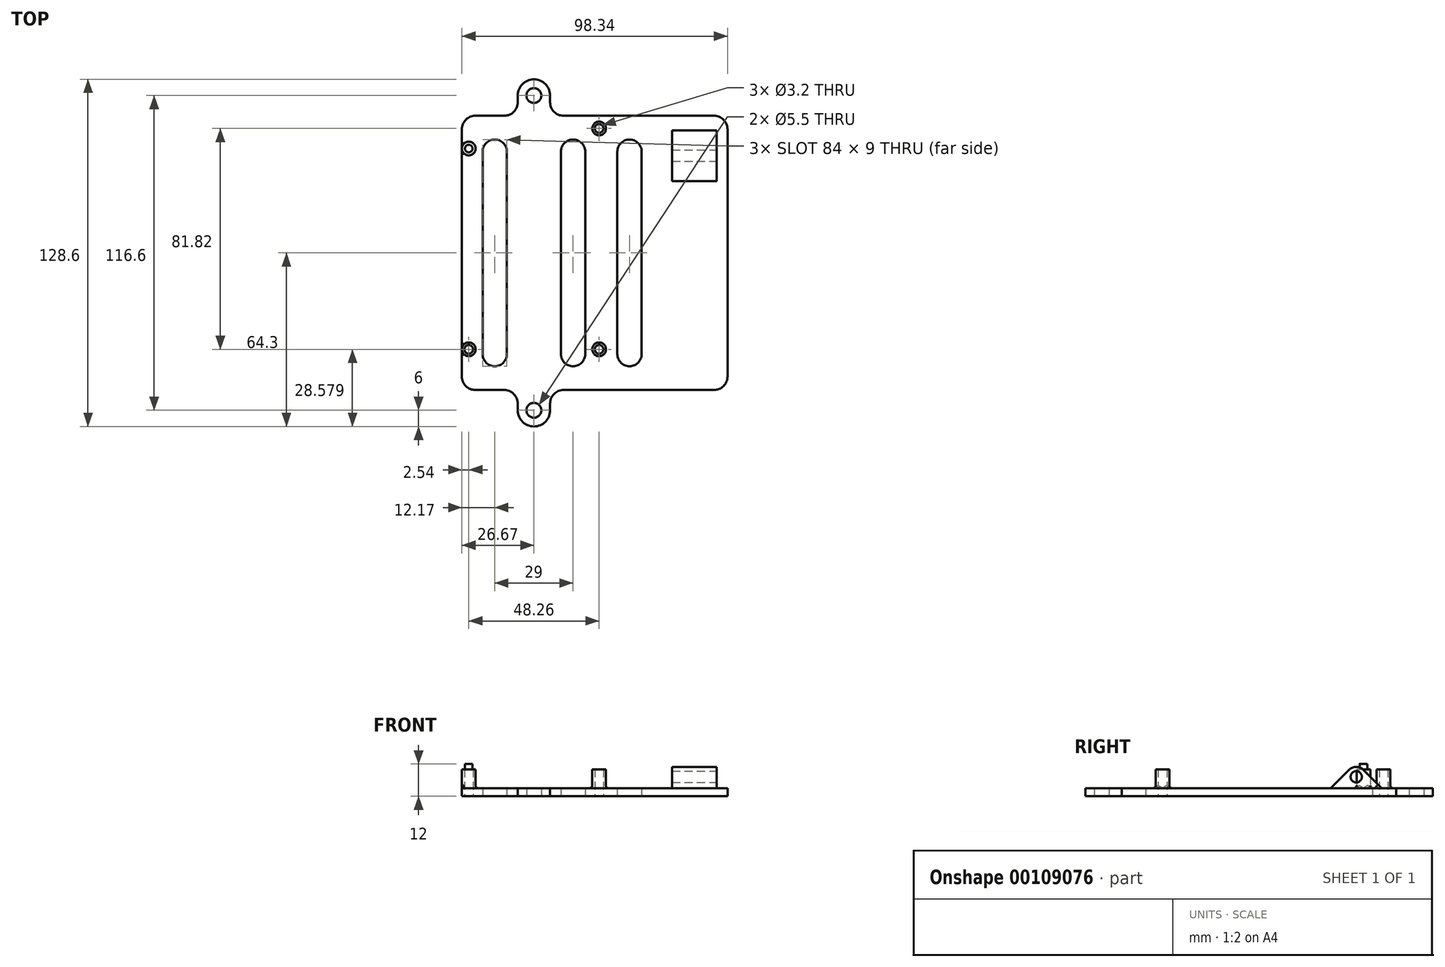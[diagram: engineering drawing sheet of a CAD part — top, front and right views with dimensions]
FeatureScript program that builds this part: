
annotation { "Feature Type Name" : "Feature", "Feature Type Description" : "" }
export const myFeature = defineFeature(function(context is Context, id is Id, definition is map)
    precondition{}
    {
        {
            var Q0;
            Q0=qCreatedBy(makeId("Top.planeOp"),FACE);
            var sketch = newSketch(context, id + "F0", { "sketchPlane" : qUnion([Q0])});
            skLineSegment(sketch, "E0.bottom", {"start": v(26.67, -50.8) * mm, "end": v(-26.67, -50.8) * mm});
            skLineSegment(sketch, "E0.top", {"start": v(26.67, 50.8) * mm, "end": v(-26.67, 50.8) * mm});
            skLineSegment(sketch, "E0.left", {"start": v(26.67, -50.8) * mm, "end": v(26.67, 50.8) * mm});
            skLineSegment(sketch, "E0.right", {"start": v(-26.67, -50.8) * mm, "end": v(-26.67, 50.8) * mm});
            skPoint(sketch, "E0.middle", {"position": v(0, 0) * mm});
            skLineSegment(sketch, "E1.bottom", {"start": v(-24.13, 46.1) * mm, "end": v(24.13, 46.1) * mm, "construction": true});
            skLineSegment(sketch, "E1.top", {"start": v(-24.13, -35.72) * mm, "end": v(24.13, -35.72) * mm, "construction": true});
            skLineSegment(sketch, "E1.left", {"start": v(-24.13, 46.1) * mm, "end": v(-24.13, -35.72) * mm, "construction": true});
            skLineSegment(sketch, "E1.right", {"start": v(24.13, 46.1) * mm, "end": v(24.13, -35.72) * mm, "construction": true});
            skPoint(sketch, "E2", {"position": v(-24.13, 38.67) * mm});
            skLineSegment(sketch, "E3", {"start": v(0, 0) * mm, "end": v(0, 72.43) * mm, "construction": true});
            skPoint(sketch, "E4", {"position": v(0, -35.72) * mm});
            skCircle(sketch, "E5", {"center": v(-24.13, -35.72) * mm, "radius": 1.6 * mm});
            skCircle(sketch, "E6", {"center": v(24.13, -35.72) * mm, "radius": 1.6 * mm});
            skCircle(sketch, "E7", {"center": v(24.13, 46.1) * mm, "radius": 1.6 * mm});
            skCircle(sketch, "E8", {"center": v(24.13, 46.1) * mm, "radius": 2.54 * mm});
            skCircle(sketch, "E9", {"center": v(-24.13, 38.67) * mm, "radius": 2.54 * mm});
            skCircle(sketch, "E10", {"center": v(24.13, -35.72) * mm, "radius": 2.54 * mm});
            skCircle(sketch, "E11", {"center": v(-24.13, -35.72) * mm, "radius": 2.54 * mm});
            skLineSegment(sketch, "E12", {"start": v(-6, 50.8) * mm, "end": v(-6, 58.3) * mm});
            skArc(sketch, "E13", {"start": v(6, 58.3) * mm, "mid": v(0, 64.3) * mm, "end": v(-6, 58.3) * mm});
            skLineSegment(sketch, "E14", {"start": v(6, 58.3) * mm, "end": v(6, 50.8) * mm});
            skCircle(sketch, "E15", {"center": v(0, 58.3) * mm, "radius": 2.75 * mm});
            skLineSegment(sketch, "E16", {"start": v(-66.86, 0) * mm, "end": v(84.73, 0) * mm, "construction": true});
            skLineSegment(sketch, "E17.MirrorCS", {"start": v(6, -58.3) * mm, "end": v(6, -50.8) * mm});
            skLineSegment(sketch, "E18.MirrorCS", {"start": v(-6, -50.8) * mm, "end": v(-6, -58.3) * mm});
            skCircle(sketch, "E19.MirrorC", {"center": v(0, -58.3) * mm, "radius": 2.75 * mm});
            skArc(sketch, "E20.MirrorCS", {"start": v(6, -58.3) * mm, "mid": v(0, -64.3) * mm, "end": v(-6, -58.3) * mm});
            skLineSegment(sketch, "E21", {"start": v(19, -37.5) * mm, "end": v(19, 37.5) * mm});
            skPoint(sketch, "E22", {"position": v(19, 0) * mm});
            skLineSegment(sketch, "E23", {"start": v(10, -37.5) * mm, "end": v(10, 37.5) * mm});
            skPoint(sketch, "E24", {"position": v(10, 0) * mm});
            skArc(sketch, "E25", {"start": v(19, -37.5) * mm, "mid": v(14.5, -42) * mm, "end": v(10, -37.5) * mm});
            skArc(sketch, "E26", {"start": v(10, 37.5) * mm, "mid": v(14.5, 42) * mm, "end": v(19, 37.5) * mm});
            skLineSegment(sketch, "E27.direction1", {"start": v(10, -37.5) * mm, "end": v(-4, -37.5) * mm, "construction": true});
            skLineSegment(sketch, "E28.bottom", {"start": v(26.67, 50.8) * mm, "end": v(71.67, 50.8) * mm});
            skLineSegment(sketch, "E28.top", {"start": v(26.67, -50.8) * mm, "end": v(71.67, -50.8) * mm});
            skLineSegment(sketch, "E28.left", {"start": v(26.67, 50.8) * mm, "end": v(26.67, -50.8) * mm});
            skLineSegment(sketch, "E28.right", {"start": v(71.67, 50.8) * mm, "end": v(71.67, -50.8) * mm});
            skLineSegment(sketch, "E29", {"start": v(30.9, -37.5) * mm, "end": v(30.9, 37.5) * mm});
            skLineSegment(sketch, "E30", {"start": v(39.9, 37.5) * mm, "end": v(39.9, -37.5) * mm});
            skArc(sketch, "E31", {"start": v(39.9, 37.5) * mm, "mid": v(35.4, 42) * mm, "end": v(30.9, 37.5) * mm});
            skArc(sketch, "E32", {"start": v(30.9, -37.5) * mm, "mid": v(35.4, -42) * mm, "end": v(39.9, -37.5) * mm});
            skLineSegment(sketch, "E33.MirrorCS", {"start": v(-10, -37.5) * mm, "end": v(-10, 37.5) * mm});
            skArc(sketch, "E34.MirrorCS", {"start": v(-10, 37.5) * mm, "mid": v(-14.5, 42) * mm, "end": v(-19, 37.5) * mm});
            skLineSegment(sketch, "E35.MirrorCS", {"start": v(-19, -37.5) * mm, "end": v(-19, 37.5) * mm});
            skArc(sketch, "E36.MirrorCS", {"start": v(-19, -37.5) * mm, "mid": v(-14.5, -42) * mm, "end": v(-10, -37.5) * mm});
            skSolve(sketch);
        }
        {
            var Q0;
            {var subQ5=sQuery(id+"F0.wireOp",EDGE,"E0.bottom");Q0=makeQuery(id+"F0.imprint","IMPRINT",FACE,{"disambiguationData":[TD([[makeQuery(id+"F0.imprint","IMPRINT",EDGE,{"derivedFrom":subQ5}),-1.0]])]});}
            var Q1;
            Q1=makeQuery(id+"F0.imprint","IMPRINT",FACE,{"disambiguationData":[TD([[makeQuery(id+"F0.imprint","IMPRINT",EDGE,{"derivedFrom":sQuery(id+"F0.wireOp",EDGE,"E5")}),-1.0]])]});
            var Q2;
            Q2=makeQuery(id+"F0.imprint","IMPRINT",FACE,{"disambiguationData":[TD([[makeQuery(id+"F0.imprint","IMPRINT",EDGE,{"derivedFrom":sQuery(id+"F0.wireOp",EDGE,"E6")}),-1.0]])]});
            var Q3;
            Q3=makeQuery(id+"F0.imprint","IMPRINT",FACE,{"disambiguationData":[TD([[makeQuery(id+"F0.imprint","IMPRINT",EDGE,{"derivedFrom":sQuery(id+"F0.wireOp",EDGE,"E7")}),-1.0]])]});
            var Q4;
            Q4=makeQuery(id+"F0.imprint","IMPRINT",FACE,{"disambiguationData":[TD([[makeQuery(id+"F0.imprint","IMPRINT",EDGE,{"derivedFrom":sQuery(id+"F0.wireOp",EDGE,"E9")}),1.0]])]});
            var Q5;
            {var subQ1=sQuery(id+"F0.wireOp",EDGE,"E12");Q5=makeQuery(id+"F0.imprint","IMPRINT",FACE,{"disambiguationData":[TD([[makeQuery(id+"F0.imprint","IMPRINT",EDGE,{"derivedFrom":subQ1}),-1.0]])]});}
            var Q6;
            {var subQ1=sQuery(id+"F0.wireOp",EDGE,"E17.MirrorCS");Q6=makeQuery(id+"F0.imprint","IMPRINT",FACE,{"disambiguationData":[TD([[makeQuery(id+"F0.imprint","IMPRINT",EDGE,{"derivedFrom":subQ1}),1.0]])]});}
            var Q7;
            {var subQ3=sQuery(id+"F0.wireOp",EDGE,"E28.bottom");Q7=makeQuery(id+"F0.imprint","IMPRINT",FACE,{"disambiguationData":[TD([[makeQuery(id+"F0.imprint","IMPRINT",EDGE,{"derivedFrom":subQ3}),-1.0]])]});}
            extrude(context, id + "F1", {"entities" : qUnion([Q0, Q1, Q2, Q3, Q4, Q5, Q6, Q7]), "depth" : 3 * mm});
        }
        {
            var Q0;
            Q0=makeQuery(id+"F0.imprint","IMPRINT",FACE,{"disambiguationData":[TD([[makeQuery(id+"F0.imprint","IMPRINT",EDGE,{"derivedFrom":sQuery(id+"F0.wireOp",EDGE,"E7")}),-1.0]])]});
            var Q1;
            Q1=makeQuery(id+"F0.imprint","IMPRINT",FACE,{"disambiguationData":[TD([[makeQuery(id+"F0.imprint","IMPRINT",EDGE,{"derivedFrom":sQuery(id+"F0.wireOp",EDGE,"E9")}),1.0]])]});
            var Q2;
            Q2=makeQuery(id+"F0.imprint","IMPRINT",FACE,{"disambiguationData":[TD([[makeQuery(id+"F0.imprint","IMPRINT",EDGE,{"derivedFrom":sQuery(id+"F0.wireOp",EDGE,"E5")}),-1.0]])]});
            var Q3;
            Q3=makeQuery(id+"F0.imprint","IMPRINT",FACE,{"disambiguationData":[TD([[makeQuery(id+"F0.imprint","IMPRINT",EDGE,{"derivedFrom":sQuery(id+"F0.wireOp",EDGE,"E6")}),-1.0]])]});
            extrude(context, id + "F2", {"entities" : qUnion([Q0, Q1, Q2, Q3]), "operationType" : NewBodyOperationType.ADD, "depth" : 10 * mm});
        }
        {
            var Q0;
            Q0=makeQuery(id+"F2.opExtrude","CAP_FACE",FACE,{"disambiguationData":[OSD([sQuery(id+"F0.wireOp",EDGE,"E9")])],"isStart":false});
            var sketch = newSketch(context, id + "F3", { "sketchPlane" : qUnion([Q0])});
            skCircle(sketch, "E37", {"center": v(-24.13, 38.67) * mm, "radius": 1.4 * mm});
            skSolve(sketch);
        }
        {
            var Q0;
            Q0 = qSketchRegion(id + "F3", true);
            extrude(context, id + "F4", {"entities" : qUnion([Q0]), "operationType" : NewBodyOperationType.ADD, "depth" : 2 * mm});
        }
        {
            var Q0;
            Q0=makeQuery(id+"F1.opExtrude","SWEPT_EDGE",EDGE,{"disambiguationData":[OSD([sQuery(id+"F0.wireOp",EDGE,"E0.top"),sQuery(id+"F0.wireOp",EDGE,"E0.left")])]});
            var Q1;
            Q1=makeQuery(id+"F1.opExtrude","SWEPT_EDGE",EDGE,{"disambiguationData":[OSD([sQuery(id+"F0.wireOp",EDGE,"E0.top"),sQuery(id+"F0.wireOp",EDGE,"E14")])]});
            var Q2;
            Q2=makeQuery(id+"F1.opExtrude","SWEPT_EDGE",EDGE,{"disambiguationData":[OSD([sQuery(id+"F0.wireOp",EDGE,"E0.top"),sQuery(id+"F0.wireOp",EDGE,"E12")])]});
            var Q3;
            Q3=makeQuery(id+"F1.opExtrude","SWEPT_EDGE",EDGE,{"disambiguationData":[OSD([sQuery(id+"F0.wireOp",EDGE,"E0.top"),sQuery(id+"F0.wireOp",EDGE,"E0.right")])]});
            var Q4;
            Q4=makeQuery(id+"F1.opExtrude","SWEPT_EDGE",EDGE,{"disambiguationData":[OSD([sQuery(id+"F0.wireOp",EDGE,"E0.bottom"),sQuery(id+"F0.wireOp",EDGE,"E0.right")])]});
            var Q5;
            Q5=makeQuery(id+"F1.opExtrude","SWEPT_EDGE",EDGE,{"disambiguationData":[OSD([sQuery(id+"F0.wireOp",EDGE,"E0.bottom"),sQuery(id+"F0.wireOp",EDGE,"E18.MirrorCS")])]});
            var Q6;
            Q6=makeQuery(id+"F1.opExtrude","SWEPT_EDGE",EDGE,{"disambiguationData":[OSD([sQuery(id+"F0.wireOp",EDGE,"E0.bottom"),sQuery(id+"F0.wireOp",EDGE,"E17.MirrorCS")])]});
            var Q7;
            Q7=makeQuery(id+"F1.opExtrude","SWEPT_EDGE",EDGE,{"disambiguationData":[OSD([sQuery(id+"F0.wireOp",EDGE,"E0.bottom"),sQuery(id+"F0.wireOp",EDGE,"E0.left")])]});
            fillet(context, id + "F5", {"entities" : qUnion([Q0, Q1, Q2, Q3, Q4, Q5, Q6, Q7]), "radius" : 5 * mm, "tangentPropagation" : true, "allowEdgeOverflow" : false});
        }
        {
            var Q0;
            Q0=makeQuery(id+"F1.opExtrude","SWEPT_FACE",FACE,{"disambiguationData":[OSD([sQuery(id+"F0.wireOp",EDGE,"E28.right")])]});
            var sketch = newSketch(context, id + "F6", { "sketchPlane" : qUnion([Q0])});
            skLineSegment(sketch, "E38.0", {"start": v(50.8, 3) * mm, "end": v(-50.8, 3) * mm, "construction": true});
            skLineSegment(sketch, "E39", {"start": v(26.57, 3) * mm, "end": v(33.38, 9.82) * mm});
            skLineSegment(sketch, "E40", {"start": v(45.43, 3) * mm, "end": v(38.62, 9.82) * mm});
            skArc(sketch, "E41", {"start": v(38.62, 9.82) * mm, "mid": v(36, 10.9) * mm, "end": v(33.38, 9.82) * mm});
            skLineSegment(sketch, "E42", {"start": v(0, 30.22) * mm, "end": v(0, -10.95) * mm, "construction": true});
            skLineSegment(sketch, "E43", {"start": v(26.57, 3) * mm, "end": v(45.43, 3) * mm});
            skArc(sketch, "E44.MirrorCS", {"start": v(-38.62, 9.82) * mm, "mid": v(-36, 10.9) * mm, "end": v(-33.38, 9.82) * mm});
            skLineSegment(sketch, "E45.MirrorCS", {"start": v(-26.57, 3) * mm, "end": v(-33.38, 9.82) * mm});
            skLineSegment(sketch, "E46.MirrorCS", {"start": v(-26.57, 3) * mm, "end": v(-45.43, 3) * mm});
            skLineSegment(sketch, "E47.MirrorCS", {"start": v(-45.43, 3) * mm, "end": v(-38.62, 9.82) * mm});
            skCircle(sketch, "E48", {"center": v(36, 7.2) * mm, "radius": 2.1 * mm});
            skCircle(sketch, "E49.MirrorC", {"center": v(-36, 7.2) * mm, "radius": 2.1 * mm});
            skSolve(sketch);
        }
        {
            var Q0;
            Q0=makeQuery(id+"F6.imprint","IMPRINT",FACE,{"disambiguationData":[TD([[makeQuery(id+"F6.imprint","IMPRINT",EDGE,{"derivedFrom":sQuery(id+"F6.wireOp",EDGE,"E39")}),-1.0]])]});
            var Q1;
            Q1=makeQuery(id+"F6.imprint","IMPRINT",FACE,{"disambiguationData":[TD([[makeQuery(id+"F6.imprint","IMPRINT",EDGE,{"derivedFrom":sQuery(id+"F6.wireOp",EDGE,"E44.MirrorCS")}),-1.0]])]});
            extrude(context, id + "F7", {"entities" : qUnion([Q0, Q1]), "operationType" : NewBodyOperationType.ADD, "oppositeDirection" : true, "depth" : 20.5 * mm, "hasSecondDirection" : true, "secondDirectionOppositeDirection" : true, "secondDirectionDepth" : 4 * mm});
        }
        {
            var Q0;
            Q0=makeQuery(id+"F1.opExtrude","SWEPT_EDGE",EDGE,{"disambiguationData":[OSD([sQuery(id+"F0.wireOp",EDGE,"E28.top"),sQuery(id+"F0.wireOp",EDGE,"E28.right")])]});
            var Q1;
            Q1=makeQuery(id+"F7.opExtrude","SWEPT_EDGE",EDGE,{"disambiguationData":[OSD([sQuery(id+"F0.wireOp",EDGE,"E28.right"),sQuery(id+"F6.wireOp",EDGE,"E46.MirrorCS"),sQuery(id+"F6.wireOp",EDGE,"E47.MirrorCS")])]});
            var Q2;
            Q2=makeQuery(id+"F7.opExtrude","SWEPT_EDGE",EDGE,{"disambiguationData":[OSD([sQuery(id+"F0.wireOp",EDGE,"E28.right"),sQuery(id+"F6.wireOp",EDGE,"E45.MirrorCS"),sQuery(id+"F6.wireOp",EDGE,"E46.MirrorCS")])]});
            var Q3;
            Q3=makeQuery(id+"F7.opExtrude","SWEPT_EDGE",EDGE,{"disambiguationData":[OSD([sQuery(id+"F0.wireOp",EDGE,"E28.right"),sQuery(id+"F6.wireOp",EDGE,"E39"),sQuery(id+"F6.wireOp",EDGE,"E43")])]});
            var Q4;
            Q4=makeQuery(id+"F7.opExtrude","SWEPT_EDGE",EDGE,{"disambiguationData":[OSD([sQuery(id+"F0.wireOp",EDGE,"E28.right"),sQuery(id+"F6.wireOp",EDGE,"E40"),sQuery(id+"F6.wireOp",EDGE,"E43")])]});
            var Q5;
            Q5=makeQuery(id+"F1.opExtrude","SWEPT_EDGE",EDGE,{"disambiguationData":[OSD([sQuery(id+"F0.wireOp",EDGE,"E28.bottom"),sQuery(id+"F0.wireOp",EDGE,"E28.right")])]});
            fillet(context, id + "F8", {"entities" : qUnion([Q0, Q1, Q2, Q3, Q4, Q5]), "radius" : 5 * mm, "tangentPropagation" : true, "allowEdgeOverflow" : false});
        }
        {
            var Q0;
            Q0=makeQuery(id+"F2.boolean.opBoolean","INTERSECT",EDGE,{"derivedFrom":[makeQuery(id+"F1.opExtrude","CAP_FACE",FACE,{"disambiguationData":[OSD([sQuery(id+"F0.wireOp",EDGE,"E0.bottom"),sQuery(id+"F0.wireOp",EDGE,"E0.top"),sQuery(id+"F0.wireOp",EDGE,"E0.right"),sQuery(id+"F0.wireOp",EDGE,"E5"),sQuery(id+"F0.wireOp",EDGE,"E6"),sQuery(id+"F0.wireOp",EDGE,"E7"),sQuery(id+"F0.wireOp",EDGE,"E12"),sQuery(id+"F0.wireOp",EDGE,"E13"),sQuery(id+"F0.wireOp",EDGE,"E14"),sQuery(id+"F0.wireOp",EDGE,"E15"),sQuery(id+"F0.wireOp",EDGE,"E17.MirrorCS"),sQuery(id+"F0.wireOp",EDGE,"E18.MirrorCS"),sQuery(id+"F0.wireOp",EDGE,"E19.MirrorC"),sQuery(id+"F0.wireOp",EDGE,"E20.MirrorCS"),sQuery(id+"F0.wireOp",EDGE,"E21"),sQuery(id+"F0.wireOp",EDGE,"E23"),sQuery(id+"F0.wireOp",EDGE,"E25"),sQuery(id+"F0.wireOp",EDGE,"E26"),sQuery(id+"F0.wireOp",EDGE,"E28.bottom"),sQuery(id+"F0.wireOp",EDGE,"E28.top"),sQuery(id+"F0.wireOp",EDGE,"E28.right"),sQuery(id+"F0.wireOp",EDGE,"E29"),sQuery(id+"F0.wireOp",EDGE,"E30"),sQuery(id+"F0.wireOp",EDGE,"E31"),sQuery(id+"F0.wireOp",EDGE,"E32"),sQuery(id+"F0.wireOp",EDGE,"E33.MirrorCS"),sQuery(id+"F0.wireOp",EDGE,"E34.MirrorCS"),sQuery(id+"F0.wireOp",EDGE,"E35.MirrorCS"),sQuery(id+"F0.wireOp",EDGE,"E36.MirrorCS")])],"isStart":false}),makeQuery(id+"F2.opExtrude","SWEPT_FACE",FACE,{"disambiguationData":[OSD([sQuery(id+"F0.wireOp",EDGE,"E10")])]})]});
            var Q1;
            Q1=makeQuery(id+"F2.boolean.opBoolean","INTERSECT",EDGE,{"derivedFrom":[makeQuery(id+"F1.opExtrude","CAP_FACE",FACE,{"disambiguationData":[OSD([sQuery(id+"F0.wireOp",EDGE,"E0.bottom"),sQuery(id+"F0.wireOp",EDGE,"E0.top"),sQuery(id+"F0.wireOp",EDGE,"E0.right"),sQuery(id+"F0.wireOp",EDGE,"E5"),sQuery(id+"F0.wireOp",EDGE,"E6"),sQuery(id+"F0.wireOp",EDGE,"E7"),sQuery(id+"F0.wireOp",EDGE,"E12"),sQuery(id+"F0.wireOp",EDGE,"E13"),sQuery(id+"F0.wireOp",EDGE,"E14"),sQuery(id+"F0.wireOp",EDGE,"E15"),sQuery(id+"F0.wireOp",EDGE,"E17.MirrorCS"),sQuery(id+"F0.wireOp",EDGE,"E18.MirrorCS"),sQuery(id+"F0.wireOp",EDGE,"E19.MirrorC"),sQuery(id+"F0.wireOp",EDGE,"E20.MirrorCS"),sQuery(id+"F0.wireOp",EDGE,"E21"),sQuery(id+"F0.wireOp",EDGE,"E23"),sQuery(id+"F0.wireOp",EDGE,"E25"),sQuery(id+"F0.wireOp",EDGE,"E26"),sQuery(id+"F0.wireOp",EDGE,"E28.bottom"),sQuery(id+"F0.wireOp",EDGE,"E28.top"),sQuery(id+"F0.wireOp",EDGE,"E28.right"),sQuery(id+"F0.wireOp",EDGE,"E29"),sQuery(id+"F0.wireOp",EDGE,"E30"),sQuery(id+"F0.wireOp",EDGE,"E31"),sQuery(id+"F0.wireOp",EDGE,"E32"),sQuery(id+"F0.wireOp",EDGE,"E33.MirrorCS"),sQuery(id+"F0.wireOp",EDGE,"E34.MirrorCS"),sQuery(id+"F0.wireOp",EDGE,"E35.MirrorCS"),sQuery(id+"F0.wireOp",EDGE,"E36.MirrorCS")])],"isStart":false}),makeQuery(id+"F2.opExtrude","SWEPT_FACE",FACE,{"disambiguationData":[OSD([sQuery(id+"F0.wireOp",EDGE,"E11")])]})]});
            var Q2;
            Q2=makeQuery(id+"F2.boolean.opBoolean","INTERSECT",EDGE,{"derivedFrom":[makeQuery(id+"F1.opExtrude","CAP_FACE",FACE,{"disambiguationData":[OSD([sQuery(id+"F0.wireOp",EDGE,"E0.bottom"),sQuery(id+"F0.wireOp",EDGE,"E0.top"),sQuery(id+"F0.wireOp",EDGE,"E0.right"),sQuery(id+"F0.wireOp",EDGE,"E5"),sQuery(id+"F0.wireOp",EDGE,"E6"),sQuery(id+"F0.wireOp",EDGE,"E7"),sQuery(id+"F0.wireOp",EDGE,"E12"),sQuery(id+"F0.wireOp",EDGE,"E13"),sQuery(id+"F0.wireOp",EDGE,"E14"),sQuery(id+"F0.wireOp",EDGE,"E15"),sQuery(id+"F0.wireOp",EDGE,"E17.MirrorCS"),sQuery(id+"F0.wireOp",EDGE,"E18.MirrorCS"),sQuery(id+"F0.wireOp",EDGE,"E19.MirrorC"),sQuery(id+"F0.wireOp",EDGE,"E20.MirrorCS"),sQuery(id+"F0.wireOp",EDGE,"E21"),sQuery(id+"F0.wireOp",EDGE,"E23"),sQuery(id+"F0.wireOp",EDGE,"E25"),sQuery(id+"F0.wireOp",EDGE,"E26"),sQuery(id+"F0.wireOp",EDGE,"E28.bottom"),sQuery(id+"F0.wireOp",EDGE,"E28.top"),sQuery(id+"F0.wireOp",EDGE,"E28.right"),sQuery(id+"F0.wireOp",EDGE,"E29"),sQuery(id+"F0.wireOp",EDGE,"E30"),sQuery(id+"F0.wireOp",EDGE,"E31"),sQuery(id+"F0.wireOp",EDGE,"E32"),sQuery(id+"F0.wireOp",EDGE,"E33.MirrorCS"),sQuery(id+"F0.wireOp",EDGE,"E34.MirrorCS"),sQuery(id+"F0.wireOp",EDGE,"E35.MirrorCS"),sQuery(id+"F0.wireOp",EDGE,"E36.MirrorCS")])],"isStart":false}),makeQuery(id+"F2.opExtrude","SWEPT_FACE",FACE,{"disambiguationData":[OSD([sQuery(id+"F0.wireOp",EDGE,"E9")])]})]});
            var Q3;
            Q3=makeQuery(id+"F2.boolean.opBoolean","INTERSECT",EDGE,{"derivedFrom":[makeQuery(id+"F1.opExtrude","CAP_FACE",FACE,{"disambiguationData":[OSD([sQuery(id+"F0.wireOp",EDGE,"E0.bottom"),sQuery(id+"F0.wireOp",EDGE,"E0.top"),sQuery(id+"F0.wireOp",EDGE,"E0.right"),sQuery(id+"F0.wireOp",EDGE,"E5"),sQuery(id+"F0.wireOp",EDGE,"E6"),sQuery(id+"F0.wireOp",EDGE,"E7"),sQuery(id+"F0.wireOp",EDGE,"E12"),sQuery(id+"F0.wireOp",EDGE,"E13"),sQuery(id+"F0.wireOp",EDGE,"E14"),sQuery(id+"F0.wireOp",EDGE,"E15"),sQuery(id+"F0.wireOp",EDGE,"E17.MirrorCS"),sQuery(id+"F0.wireOp",EDGE,"E18.MirrorCS"),sQuery(id+"F0.wireOp",EDGE,"E19.MirrorC"),sQuery(id+"F0.wireOp",EDGE,"E20.MirrorCS"),sQuery(id+"F0.wireOp",EDGE,"E21"),sQuery(id+"F0.wireOp",EDGE,"E23"),sQuery(id+"F0.wireOp",EDGE,"E25"),sQuery(id+"F0.wireOp",EDGE,"E26"),sQuery(id+"F0.wireOp",EDGE,"E28.bottom"),sQuery(id+"F0.wireOp",EDGE,"E28.top"),sQuery(id+"F0.wireOp",EDGE,"E28.right"),sQuery(id+"F0.wireOp",EDGE,"E29"),sQuery(id+"F0.wireOp",EDGE,"E30"),sQuery(id+"F0.wireOp",EDGE,"E31"),sQuery(id+"F0.wireOp",EDGE,"E32"),sQuery(id+"F0.wireOp",EDGE,"E33.MirrorCS"),sQuery(id+"F0.wireOp",EDGE,"E34.MirrorCS"),sQuery(id+"F0.wireOp",EDGE,"E35.MirrorCS"),sQuery(id+"F0.wireOp",EDGE,"E36.MirrorCS")])],"isStart":false}),makeQuery(id+"F2.opExtrude","SWEPT_FACE",FACE,{"disambiguationData":[OSD([sQuery(id+"F0.wireOp",EDGE,"E8")])]})]});
            fillet(context, id + "F9", {"entities" : qUnion([Q0, Q1, Q2, Q3]), "radius" : 1 * mm, "tangentPropagation" : true, "allowEdgeOverflow" : false});
        }
    });
